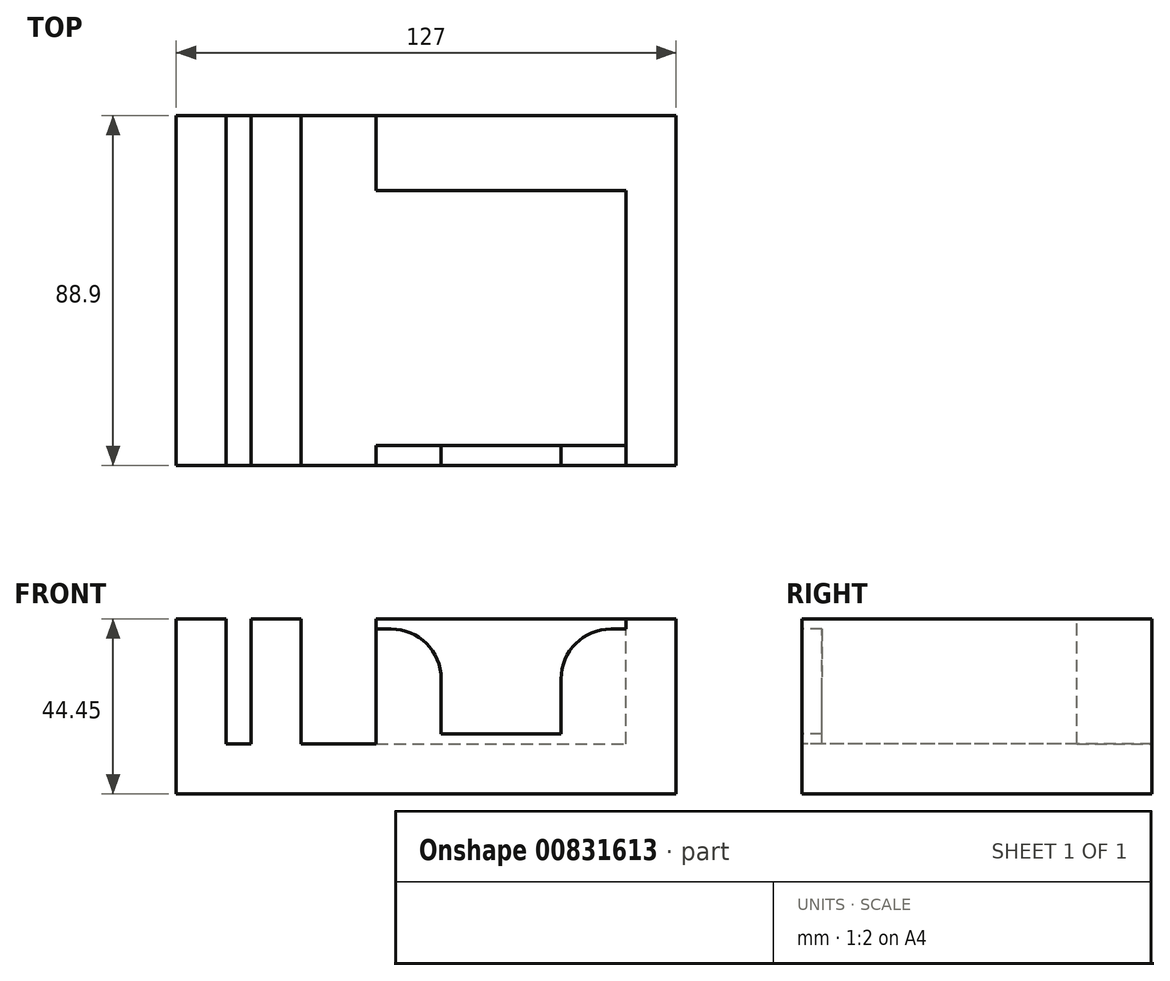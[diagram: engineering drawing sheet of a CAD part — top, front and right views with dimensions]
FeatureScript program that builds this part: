
annotation { "Feature Type Name" : "Feature", "Feature Type Description" : "" }
export const myFeature = defineFeature(function(context is Context, id is Id, definition is map)
    precondition{}
    {
        {
            var Q0;
            Q0=qCreatedBy(makeId("Front.planeOp"),FACE);
            var sketch = newSketch(context, id + "F0", { "sketchPlane" : qUnion([Q0])});
            skLineSegment(sketch, "E0.bottom", {"start": v(0, 0) * mm, "end": v(127, 0) * mm});
            skLineSegment(sketch, "E0.top", {"start": v(0, 12.7) * mm, "end": v(127, 12.7) * mm});
            skLineSegment(sketch, "E0.left", {"start": v(0, 0) * mm, "end": v(0, 12.7) * mm});
            skLineSegment(sketch, "E0.right", {"start": v(127, 0) * mm, "end": v(127, 12.7) * mm});
            skSolve(sketch);
        }
        {
            var Q0;
            Q0=makeQuery(id+"F0.imprint","IMPRINT",FACE,{"disambiguationData":[TD([[makeQuery(id+"F0.imprint","IMPRINT",EDGE,{"derivedFrom":sQuery(id+"F0.wireOp",EDGE,"E0.bottom")}),1.0]])]});
            extrude(context, id + "F1", {"entities" : qUnion([Q0]), "depth" : 88.9 * mm, "offsetDistance" : 25.4 * mm});
        }
        {
            var Q0;
            Q0=makeQuery(id+"F1.opExtrude","CAP_FACE",FACE,{"disambiguationData":[OSD([sQuery(id+"F0.wireOp",EDGE,"E0.bottom"),sQuery(id+"F0.wireOp",EDGE,"E0.top"),sQuery(id+"F0.wireOp",EDGE,"E0.left"),sQuery(id+"F0.wireOp",EDGE,"E0.right")])],"isStart":false});
            var sketch = newSketch(context, id + "F2", { "sketchPlane" : qUnion([Q0])});
            skLineSegment(sketch, "E1.bottom", {"start": v(0, 12.7) * mm, "end": v(6.35, 12.7) * mm});
            skLineSegment(sketch, "E1.top", {"start": v(0, 44.45) * mm, "end": v(6.35, 44.45) * mm});
            skLineSegment(sketch, "E1.left", {"start": v(0, 12.7) * mm, "end": v(0, 44.45) * mm});
            skLineSegment(sketch, "E2.bottom", {"start": v(6.35, 44.45) * mm, "end": v(12.7, 44.45) * mm});
            skLineSegment(sketch, "E2.top", {"start": v(6.35, 12.7) * mm, "end": v(12.7, 12.7) * mm});
            skLineSegment(sketch, "E2.right", {"start": v(12.7, 44.45) * mm, "end": v(12.7, 12.7) * mm});
            skLineSegment(sketch, "E3", {"start": v(12.7, 12.7) * mm, "end": v(19.05, 12.7) * mm});
            skLineSegment(sketch, "E4", {"start": v(19.05, 12.7) * mm, "end": v(19.05, 44.45) * mm});
            skLineSegment(sketch, "E5", {"start": v(19.05, 44.45) * mm, "end": v(31.75, 44.45) * mm});
            skLineSegment(sketch, "E6", {"start": v(31.75, 44.45) * mm, "end": v(31.75, 12.7) * mm});
            skLineSegment(sketch, "E7", {"start": v(31.75, 12.7) * mm, "end": v(19.05, 12.7) * mm});
            skLineSegment(sketch, "E8", {"start": v(31.75, 12.7) * mm, "end": v(38.1, 12.7) * mm});
            skLineSegment(sketch, "E9", {"start": v(38.1, 12.7) * mm, "end": v(38.1, 44.45) * mm});
            skLineSegment(sketch, "E10", {"start": v(38.1, 44.45) * mm, "end": v(38.1, 12.7) * mm});
            skLineSegment(sketch, "E11", {"start": v(38.1, 12.7) * mm, "end": v(50.8, 12.7) * mm});
            skLineSegment(sketch, "E12", {"start": v(50.8, 12.7) * mm, "end": v(50.8, 44.45) * mm});
            skLineSegment(sketch, "E13", {"start": v(50.8, 44.45) * mm, "end": v(38.1, 44.45) * mm});
            skLineSegment(sketch, "E14.bottom", {"start": v(127, 12.7) * mm, "end": v(114.3, 12.7) * mm});
            skLineSegment(sketch, "E14.top", {"start": v(127, 44.45) * mm, "end": v(114.3, 44.45) * mm});
            skLineSegment(sketch, "E14.left", {"start": v(127, 12.7) * mm, "end": v(127, 44.45) * mm});
            skLineSegment(sketch, "E14.right", {"start": v(114.3, 12.7) * mm, "end": v(114.3, 44.45) * mm});
            skSolve(sketch);
        }
        {
            var Q0;
            Q0=makeQuery(id+"F2.imprint","IMPRINT",FACE,{"disambiguationData":[TD([[makeQuery(id+"F2.imprint","IMPRINT",EDGE,{"derivedFrom":sQuery(id+"F2.wireOp",EDGE,"E1.bottom")}),1.0]])]});
            var Q1;
            Q1=makeQuery(id+"F2.imprint","IMPRINT",FACE,{"disambiguationData":[TD([[makeQuery(id+"F2.imprint","IMPRINT",EDGE,{"derivedFrom":sQuery(id+"F2.wireOp",EDGE,"E4")}),-1.0]])]});
            var Q2;
            Q2=makeQuery(id+"F2.imprint","IMPRINT",FACE,{"disambiguationData":[TD([[makeQuery(id+"F2.imprint","IMPRINT",EDGE,{"derivedFrom":sQuery(id+"F2.wireOp",EDGE,"E10")}),1.0]])]});
            var Q3;
            Q3=makeQuery(id+"F2.imprint","IMPRINT",FACE,{"disambiguationData":[TD([[makeQuery(id+"F2.imprint","IMPRINT",EDGE,{"derivedFrom":sQuery(id+"F2.wireOp",EDGE,"E14.bottom")}),1.0]])]});
            extrude(context, id + "F3", {"entities" : qUnion([Q0, Q1, Q2, Q3]), "operationType" : NewBodyOperationType.ADD, "oppositeDirection" : true, "depth" : 88.9 * mm, "offsetDistance" : 25.4 * mm});
        }
        {
            var Q0;
            Q0=makeQuery(id+"F3.boolean.opBoolean","MERGE",FACE,{"derivedFrom":[makeQuery(id+"F1.opExtrude","CAP_FACE",FACE,{"disambiguationData":[OSD([sQuery(id+"F0.wireOp",EDGE,"E0.bottom"),sQuery(id+"F0.wireOp",EDGE,"E0.top"),sQuery(id+"F0.wireOp",EDGE,"E0.left"),sQuery(id+"F0.wireOp",EDGE,"E0.right")])],"isStart":false}),makeQuery(id+"F3.opExtrude","CAP_FACE",FACE,{"disambiguationData":[OSD([sQuery(id+"F2.wireOp",EDGE,"E1.bottom"),sQuery(id+"F2.wireOp",EDGE,"E1.top"),sQuery(id+"F2.wireOp",EDGE,"E1.left"),sQuery(id+"F2.wireOp",EDGE,"E2.bottom"),sQuery(id+"F2.wireOp",EDGE,"E2.top"),sQuery(id+"F2.wireOp",EDGE,"E2.right")])],"isStart":true}),makeQuery(id+"F3.opExtrude","CAP_FACE",FACE,{"disambiguationData":[OSD([sQuery(id+"F2.wireOp",EDGE,"E4"),sQuery(id+"F2.wireOp",EDGE,"E5"),sQuery(id+"F2.wireOp",EDGE,"E6"),sQuery(id+"F2.wireOp",EDGE,"E7")])],"isStart":true}),makeQuery(id+"F3.opExtrude","CAP_FACE",FACE,{"disambiguationData":[OSD([sQuery(id+"F2.wireOp",EDGE,"E10"),sQuery(id+"F2.wireOp",EDGE,"E11"),sQuery(id+"F2.wireOp",EDGE,"E12"),sQuery(id+"F2.wireOp",EDGE,"E13")])],"isStart":true}),makeQuery(id+"F3.opExtrude","CAP_FACE",FACE,{"disambiguationData":[OSD([sQuery(id+"F2.wireOp",EDGE,"E14.bottom"),sQuery(id+"F2.wireOp",EDGE,"E14.top"),sQuery(id+"F2.wireOp",EDGE,"E14.left"),sQuery(id+"F2.wireOp",EDGE,"E14.right")])],"isStart":true})]});
            var sketch = newSketch(context, id + "F4", { "sketchPlane" : qUnion([Q0])});
            skLineSegment(sketch, "E15.bottom", {"start": v(50.8, 12.7) * mm, "end": v(67.31, 12.7) * mm});
            skLineSegment(sketch, "E15.top", {"start": v(50.8, 41.91) * mm, "end": v(67.31, 41.91) * mm});
            skLineSegment(sketch, "E15.left", {"start": v(50.8, 12.7) * mm, "end": v(50.8, 41.91) * mm});
            skLineSegment(sketch, "E15.right", {"start": v(67.31, 12.7) * mm, "end": v(67.31, 41.91) * mm});
            skLineSegment(sketch, "E16.bottom", {"start": v(114.3, 12.7) * mm, "end": v(97.8, 12.7) * mm});
            skLineSegment(sketch, "E16.top", {"start": v(114.3, 41.91) * mm, "end": v(97.8, 41.91) * mm});
            skLineSegment(sketch, "E16.left", {"start": v(114.3, 12.7) * mm, "end": v(114.3, 41.91) * mm});
            skLineSegment(sketch, "E16.right", {"start": v(97.8, 12.7) * mm, "end": v(97.8, 41.91) * mm});
            skSolve(sketch);
        }
        {
            var Q0;
            Q0=makeQuery(id+"F4.imprint","IMPRINT",FACE,{"disambiguationData":[TD([[makeQuery(id+"F4.imprint","IMPRINT",EDGE,{"derivedFrom":sQuery(id+"F4.wireOp",EDGE,"E15.bottom")}),1.0]])]});
            var Q1;
            Q1=makeQuery(id+"F4.imprint","IMPRINT",FACE,{"disambiguationData":[TD([[makeQuery(id+"F4.imprint","IMPRINT",EDGE,{"derivedFrom":sQuery(id+"F4.wireOp",EDGE,"E16.bottom")}),1.0]])]});
            extrude(context, id + "F5", {"entities" : qUnion([Q0, Q1]), "operationType" : NewBodyOperationType.ADD, "oppositeDirection" : true, "depth" : 5.08 * mm, "offsetDistance" : 25.4 * mm});
        }
        {
            var Q0;
            Q0=makeQuery(id+"F3.boolean.opBoolean","MERGE",FACE,{"derivedFrom":[makeQuery(id+"F1.opExtrude","CAP_FACE",FACE,{"disambiguationData":[OSD([sQuery(id+"F0.wireOp",EDGE,"E0.bottom"),sQuery(id+"F0.wireOp",EDGE,"E0.top"),sQuery(id+"F0.wireOp",EDGE,"E0.left"),sQuery(id+"F0.wireOp",EDGE,"E0.right")])],"isStart":true}),makeQuery(id+"F3.opExtrude","CAP_FACE",FACE,{"disambiguationData":[OSD([sQuery(id+"F2.wireOp",EDGE,"E1.bottom"),sQuery(id+"F2.wireOp",EDGE,"E1.top"),sQuery(id+"F2.wireOp",EDGE,"E1.left"),sQuery(id+"F2.wireOp",EDGE,"E2.bottom"),sQuery(id+"F2.wireOp",EDGE,"E2.top"),sQuery(id+"F2.wireOp",EDGE,"E2.right")])],"isStart":false}),makeQuery(id+"F3.opExtrude","CAP_FACE",FACE,{"disambiguationData":[OSD([sQuery(id+"F2.wireOp",EDGE,"E4"),sQuery(id+"F2.wireOp",EDGE,"E5"),sQuery(id+"F2.wireOp",EDGE,"E6"),sQuery(id+"F2.wireOp",EDGE,"E7")])],"isStart":false}),makeQuery(id+"F3.opExtrude","CAP_FACE",FACE,{"disambiguationData":[OSD([sQuery(id+"F2.wireOp",EDGE,"E10"),sQuery(id+"F2.wireOp",EDGE,"E11"),sQuery(id+"F2.wireOp",EDGE,"E12"),sQuery(id+"F2.wireOp",EDGE,"E13")])],"isStart":false}),makeQuery(id+"F3.opExtrude","CAP_FACE",FACE,{"disambiguationData":[OSD([sQuery(id+"F2.wireOp",EDGE,"E14.bottom"),sQuery(id+"F2.wireOp",EDGE,"E14.top"),sQuery(id+"F2.wireOp",EDGE,"E14.left"),sQuery(id+"F2.wireOp",EDGE,"E14.right")])],"isStart":false})]});
            var sketch = newSketch(context, id + "F6", { "sketchPlane" : qUnion([Q0])});
            skLineSegment(sketch, "E17.bottom", {"start": v(-114.3, 12.7) * mm, "end": v(-50.8, 12.7) * mm});
            skLineSegment(sketch, "E17.top", {"start": v(-114.3, 44.45) * mm, "end": v(-50.8, 44.45) * mm});
            skLineSegment(sketch, "E17.left", {"start": v(-114.3, 12.7) * mm, "end": v(-114.3, 44.45) * mm});
            skLineSegment(sketch, "E17.right", {"start": v(-50.8, 12.7) * mm, "end": v(-50.8, 44.45) * mm});
            skSolve(sketch);
        }
        {
            var Q0;
            Q0=makeQuery(id+"F6.imprint","IMPRINT",FACE,{"disambiguationData":[TD([[makeQuery(id+"F6.imprint","IMPRINT",EDGE,{"derivedFrom":sQuery(id+"F6.wireOp",EDGE,"E17.bottom")}),-1.0]])]});
            extrude(context, id + "F7", {"entities" : qUnion([Q0]), "operationType" : NewBodyOperationType.ADD, "oppositeDirection" : true, "depth" : 19.05 * mm, "offsetDistance" : 25.4 * mm});
        }
        {
            var Q0;
            Q0=makeQuery(id+"F5.boolean.opBoolean","MERGE",FACE,{"derivedFrom":[makeQuery(id+"F3.boolean.opBoolean","MERGE",FACE,{"derivedFrom":[makeQuery(id+"F1.opExtrude","CAP_FACE",FACE,{"disambiguationData":[OSD([sQuery(id+"F0.wireOp",EDGE,"E0.bottom"),sQuery(id+"F0.wireOp",EDGE,"E0.top"),sQuery(id+"F0.wireOp",EDGE,"E0.left"),sQuery(id+"F0.wireOp",EDGE,"E0.right")])],"isStart":false}),makeQuery(id+"F3.opExtrude","CAP_FACE",FACE,{"disambiguationData":[OSD([sQuery(id+"F2.wireOp",EDGE,"E1.bottom"),sQuery(id+"F2.wireOp",EDGE,"E1.top"),sQuery(id+"F2.wireOp",EDGE,"E1.left"),sQuery(id+"F2.wireOp",EDGE,"E2.bottom"),sQuery(id+"F2.wireOp",EDGE,"E2.top"),sQuery(id+"F2.wireOp",EDGE,"E2.right")])],"isStart":true}),makeQuery(id+"F3.opExtrude","CAP_FACE",FACE,{"disambiguationData":[OSD([sQuery(id+"F2.wireOp",EDGE,"E4"),sQuery(id+"F2.wireOp",EDGE,"E5"),sQuery(id+"F2.wireOp",EDGE,"E6"),sQuery(id+"F2.wireOp",EDGE,"E7")])],"isStart":true}),makeQuery(id+"F3.opExtrude","CAP_FACE",FACE,{"disambiguationData":[OSD([sQuery(id+"F2.wireOp",EDGE,"E10"),sQuery(id+"F2.wireOp",EDGE,"E11"),sQuery(id+"F2.wireOp",EDGE,"E12"),sQuery(id+"F2.wireOp",EDGE,"E13")])],"isStart":true}),makeQuery(id+"F3.opExtrude","CAP_FACE",FACE,{"disambiguationData":[OSD([sQuery(id+"F2.wireOp",EDGE,"E14.bottom"),sQuery(id+"F2.wireOp",EDGE,"E14.top"),sQuery(id+"F2.wireOp",EDGE,"E14.left"),sQuery(id+"F2.wireOp",EDGE,"E14.right")])],"isStart":true})]}),makeQuery(id+"F5.opExtrude","CAP_FACE",FACE,{"disambiguationData":[OSD([sQuery(id+"F4.wireOp",EDGE,"E15.bottom"),sQuery(id+"F4.wireOp",EDGE,"E15.top"),sQuery(id+"F4.wireOp",EDGE,"E15.left"),sQuery(id+"F4.wireOp",EDGE,"E15.right")])],"isStart":true}),makeQuery(id+"F5.opExtrude","CAP_FACE",FACE,{"disambiguationData":[OSD([sQuery(id+"F4.wireOp",EDGE,"E16.bottom"),sQuery(id+"F4.wireOp",EDGE,"E16.top"),sQuery(id+"F4.wireOp",EDGE,"E16.left"),sQuery(id+"F4.wireOp",EDGE,"E16.right")])],"isStart":true})]});
            var sketch = newSketch(context, id + "F8", { "sketchPlane" : qUnion([Q0])});
            skLineSegment(sketch, "E18.bottom", {"start": v(67.31, 12.7) * mm, "end": v(97.8, 12.7) * mm});
            skLineSegment(sketch, "E18.top", {"start": v(67.31, 15.24) * mm, "end": v(97.8, 15.24) * mm});
            skLineSegment(sketch, "E18.left", {"start": v(67.31, 12.7) * mm, "end": v(67.31, 15.24) * mm});
            skLineSegment(sketch, "E18.right", {"start": v(97.8, 12.7) * mm, "end": v(97.8, 15.24) * mm});
            skSolve(sketch);
        }
        {
            var Q0;
            Q0=makeQuery(id+"F8.imprint","IMPRINT",FACE,{"disambiguationData":[TD([[makeQuery(id+"F8.imprint","IMPRINT",EDGE,{"derivedFrom":sQuery(id+"F8.wireOp",EDGE,"E18.bottom")}),1.0]])]});
            extrude(context, id + "F9", {"entities" : qUnion([Q0]), "operationType" : NewBodyOperationType.ADD, "oppositeDirection" : true, "depth" : 5.08 * mm, "offsetDistance" : 25.4 * mm});
        }
        {
            var Q0;
            Q0=makeQuery(id+"F5.opExtrude","SWEPT_EDGE",EDGE,{"disambiguationData":[OSD([sQuery(id+"F4.wireOp",EDGE,"E15.top"),sQuery(id+"F4.wireOp",EDGE,"E15.right")])]});
            var Q1;
            Q1=makeQuery(id+"F5.opExtrude","SWEPT_EDGE",EDGE,{"disambiguationData":[OSD([sQuery(id+"F4.wireOp",EDGE,"E16.top"),sQuery(id+"F4.wireOp",EDGE,"E16.right")])]});
            fillet(context, id + "F10", {"entities" : qUnion([Q0, Q1]), "radius" : 12.7 * mm, "tangentPropagation" : true, "allowEdgeOverflow" : false});
        }
    });
